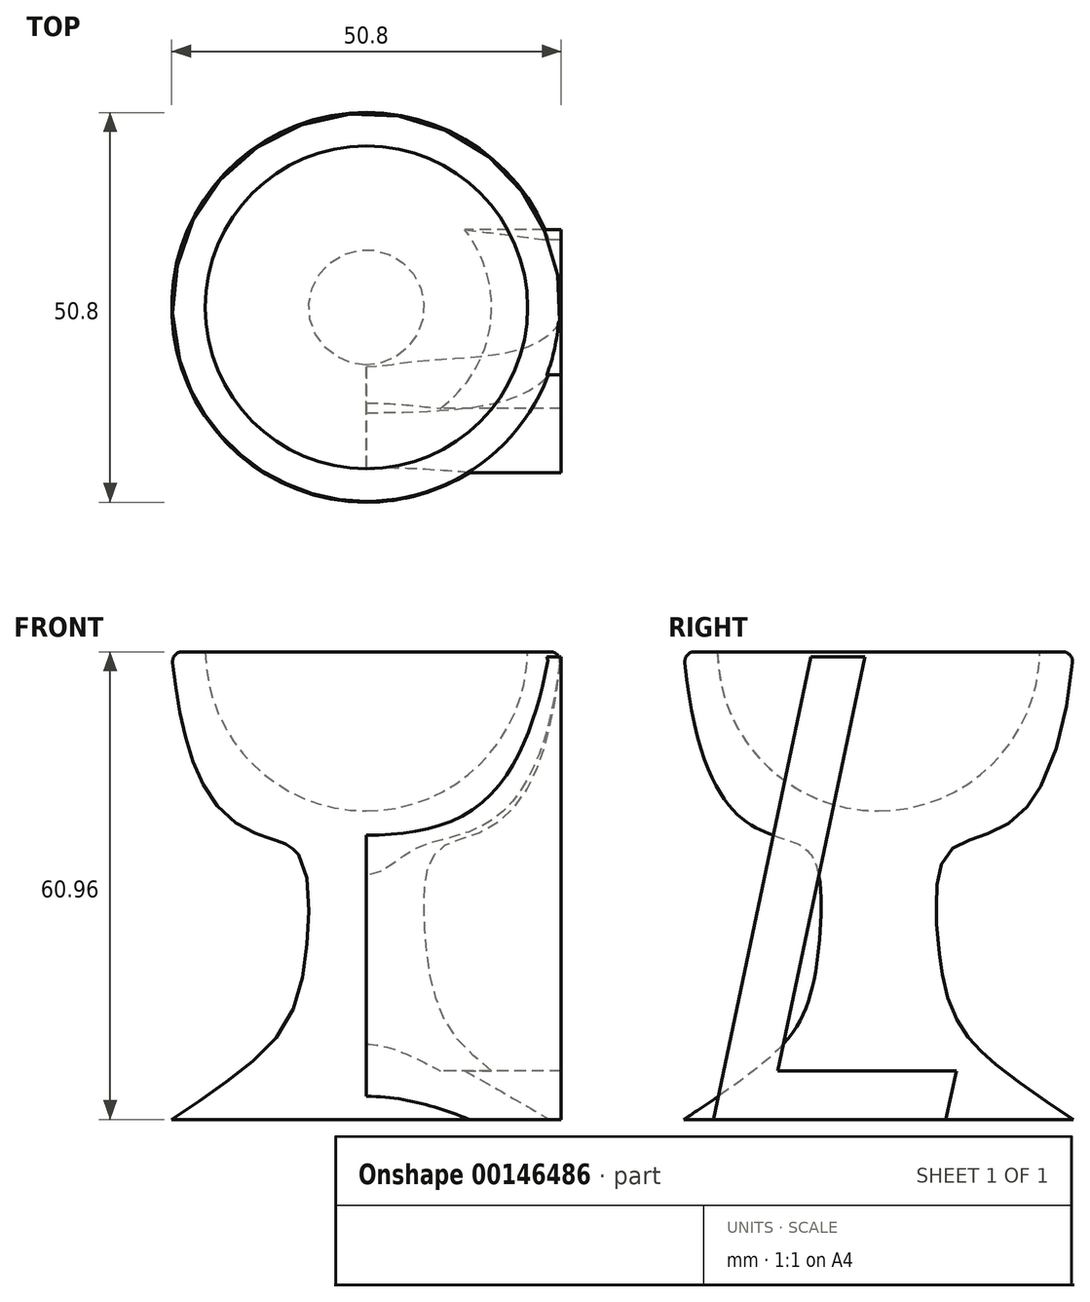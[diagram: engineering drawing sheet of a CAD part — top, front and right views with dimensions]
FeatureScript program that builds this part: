
annotation { "Feature Type Name" : "Feature", "Feature Type Description" : "" }
export const myFeature = defineFeature(function(context is Context, id is Id, definition is map)
    precondition{}
    {
        {
            var Q0;
            Q0=qCreatedBy(makeId("Top.planeOp"),FACE);
            var sketch = newSketch(context, id + "F0", { "sketchPlane" : qUnion([Q0])});
            skCircle(sketch, "E0", {"center": v(0, 0) * mm, "radius": 25.4 * mm});
            skSolve(sketch);
        }
        {
            var Q0;
            Q0 = qSketchRegion(id + "F0", true);
            extrude(context, id + "F1", {"entities" : qUnion([Q0]), "depth" : 60.96 * mm});
        }
        {
            var Q0;
            Q0=qCreatedBy(makeId("Right.planeOp"),FACE);
            var sketch = newSketch(context, id + "F2", { "sketchPlane" : qUnion([Q0])});
            skLineSegment(sketch, "E1", {"start": v(-25.4, 63.68) * mm, "end": v(-25.4, -12.25) * mm});
            skLineSegment(sketch, "E2", {"start": v(0, 65.93) * mm, "end": v(0, -16.33) * mm, "construction": true});
            skLineSegment(sketch, "E3", {"start": v(-68.17, 60.96) * mm, "end": v(41.23, 60.96) * mm, "construction": true});
            skFitSpline(sketch, "E4", {"points": [v(-25.4, 60.96) * mm, v(-9.6, 35.31) * mm, v(-7.55, 26.13) * mm, v(-9.6, 14.29) * mm, v(-25.4, 0) * mm], "startDerivative": vector(21.1, -239.08) * mm, "endDerivative": vector(-115.96, -76.68) * mm});
            skSolve(sketch);
        }
        {
            var Q0;
            Q0 = qSketchRegion(id + "F2", true);
            var Q1;
            Q1=sQuery(id+"F2.wireOp",EDGE,"E2");
            revolve(context, id + "F3", {"operationType" : NewBodyOperationType.REMOVE, "entities" : qUnion([Q0]), "axis" : qUnion([Q1]), "revolveType" : RevolveType.FULL, "oppositeDirection" : true});
        }
        {
            var Q0;
            Q0=qCreatedBy(makeId("Right.planeOp"),FACE);
            var sketch = newSketch(context, id + "F4", { "sketchPlane" : qUnion([Q0])});
            skText(sketch, "E5", { "text": "L", "fontName": "OpenSans-Italic.ttf"});
            const initialGuessF4  = {"E5": [-0.0251, 0, 1, 0, 0.06082]};
            skSetInitialGuess(sketch, initialGuessF4);
            skSolve(sketch);
        }
        {
            var Q0;
            Q0 = qSketchRegion(id + "F4", true);
            extrude(context, id + "F5", {"entities" : qUnion([Q0]), "operationType" : NewBodyOperationType.ADD, "depth" : 25.4 * mm});
        }
        {
            var Q0;
            Q0=qCreatedBy(makeId("Right.planeOp"),FACE);
            var sketch = newSketch(context, id + "F6", { "sketchPlane" : qUnion([Q0])});
            skArc(sketch, "E6", {"start": v(0, 40.2) * mm, "mid": v(21.02, 61.23) * mm, "end": v(0, 82.26) * mm});
            skLineSegment(sketch, "E7", {"start": v(0, 82.26) * mm, "end": v(0, 40.2) * mm});
            skSolve(sketch);
        }
        {
            var Q0;
            Q0 = qSketchRegion(id + "F6", true);
            var Q1;
            Q1=sQuery(id+"F6.wireOp",EDGE,"E7");
            revolve(context, id + "F7", {"operationType" : NewBodyOperationType.REMOVE, "entities" : qUnion([Q0]), "axis" : qUnion([Q1]), "revolveType" : RevolveType.FULL, "oppositeDirection" : true});
        }
        {
            var Q0;
            {var subQ0=sQuery(id+"F2.wireOp",EDGE,"E4");var subQ1=sQuery(id+"F2.wireOp",EDGE,"E1");Q0=makeQuery(id+"F3.boolean.opBoolean","MERGE",EDGE,{"derivedFrom":[makeQuery(id+"F1.opExtrude","CAP_EDGE",EDGE,{"disambiguationData":[OSD([sQuery(id+"F0.wireOp",EDGE,"E0")])],"isStart":false}),makeQuery(id+"F3.opRevolve","SWEPT_EDGE",EDGE,{"disambiguationData":[OSD([subQ1,subQ0]),TDD([makeQuery(id+"F2.imprint","INTERSECT",VERTEX,{"disambiguationData":[OD(0.0)],"derivedFrom":[subQ1,subQ0]})])]})]});}
            fillet(context, id + "F8", {"entities" : qUnion([Q0]), "radius" : 1.27 * mm, "allowEdgeOverflow" : false});
        }
    });
